# Revit family: Sanitary_Bath-Spas_AXOR_42005XXX-AXOR-Universal-Basins-Bathtubs_NEW
name_source: partatom
category: Plumbing Fixtures
revit_build: Autodesk Revit 2018 (Build: 20170223_1515(x64)
units: mm (PartAtom-declared; Revit-internal decimal feet)

## family parameters
Cut with Voids When Loaded = Yes
Host = Face
OmniClass Number = 23.31.15.11
OmniClass Title = Bath Shower Units
Part Type = Normal
Room Calculation Point = No
Round Connector Dimension = Use Diameter
Shared = No

## types (1)
- Default - please load Revit Family Type Catalog
    Always visible = Yes
    BIMobject category = Bath & Spas
    Connector Description = Water Outlet 50 mm
    Default Elevation = 1219 mm
    Description = AXOR Universal Basins & Bathtubs Bathtub 1900/850
    Design country = Germany
    Diameter = 50 mm  [stored 0.164042 ft]
    Edition number = 1
    IFC Classification = Sanitary Terminal
    Manufacturer = AXOR
    Manufacturer country = Germany
    Manufacturer name = AXOR
    Masterformat 2014 Code = 22 41 39
    Masterformat 2014 Description = Residential Faucets, Supplies, and Trim
    Material = AXOR - Ceramic - White
    Material 1 = AXOR - Metal - 000 Chrome
    Model = 42005XXX
    OmniClass Code = 23-31 15 11
    OmniClass Description = Bath Shower Units
    Product Guid = a586715b-34e5-43fb-b68c-0bf5936ce58e
    Product SKU = 42005XXX
    Product data url = https://bimobject.com
    Product family = AXOR Universal Basins & Bathtub
    Product group = Bathtub
    Product name = 42005XXX AXOR Universal Basins & Bathtubs Bathtub 1900/850
    Product url = https://www.axor-design.com
    QR code = https://bimobject.com
    UNSPSC Code = 301815
    URL = https://www.axor-design.com
    Uniclass 2015 Code = Pr_40_20_87
    Uniclass 2015 Name = Taps and water supply outlet fittings
    Uniformat II Code = D2010
    Uniformat II Description = Plumbing Fixtures
    Version = 1
    Weight Net (Kg) = 2.4

note: [stored X ft] marks values corroborated as IEEE doubles in the binary element streams (Revit-internal decimal feet)

## geometry (parser evidence)
native form markers: Sweep x2
no freeform markers — native parametric forms only
